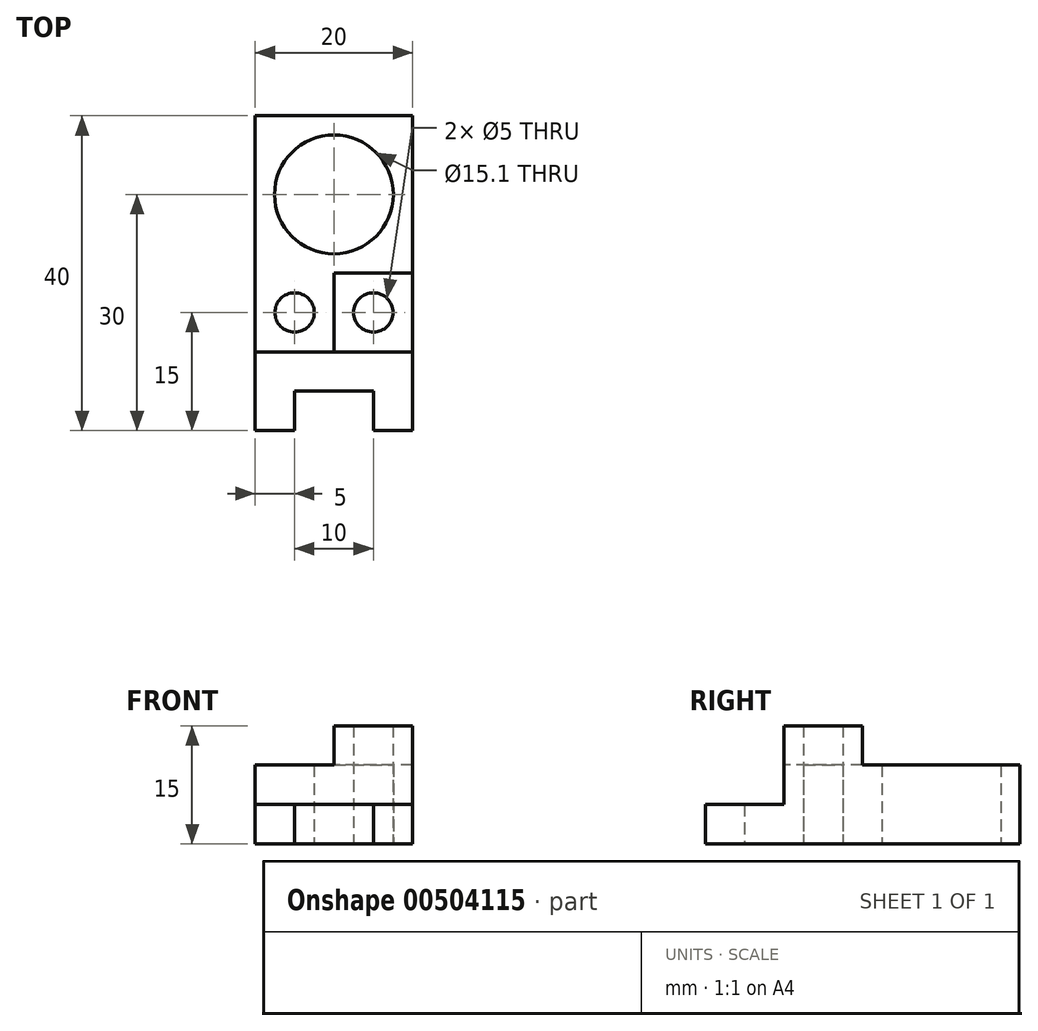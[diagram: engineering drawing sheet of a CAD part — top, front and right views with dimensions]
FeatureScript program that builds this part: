
annotation { "Feature Type Name" : "Feature", "Feature Type Description" : "" }
export const myFeature = defineFeature(function(context is Context, id is Id, definition is map)
    precondition{}
    {
        {
            var Q0;
            Q0=qCreatedBy(makeId("Top.planeOp"),FACE);
            var sketch = newSketch(context, id + "F0", { "sketchPlane" : qUnion([Q0])});
            skLineSegment(sketch, "E0.bottom", {"start": v(10, 10) * mm, "end": v(-10, 10) * mm});
            skLineSegment(sketch, "E0.top", {"start": v(10, -10) * mm, "end": v(-10, -10) * mm});
            skLineSegment(sketch, "E0.left", {"start": v(10, 10) * mm, "end": v(10, -10) * mm});
            skLineSegment(sketch, "E0.right", {"start": v(-10, 10) * mm, "end": v(-10, -10) * mm});
            skPoint(sketch, "E0.middle", {"position": v(0, 0) * mm});
            skCircle(sketch, "E1", {"center": v(0, 0) * mm, "radius": 7.55 * mm});
            skLineSegment(sketch, "E2", {"start": v(-10, -10) * mm, "end": v(-10, -20) * mm});
            skLineSegment(sketch, "E3", {"start": v(-10, -20) * mm, "end": v(10, -20) * mm});
            skLineSegment(sketch, "E4", {"start": v(10, -20) * mm, "end": v(10, -10) * mm});
            skLineSegment(sketch, "E5", {"start": v(0, -10) * mm, "end": v(0, -20) * mm});
            skLineSegment(sketch, "E6", {"start": v(-10, -20) * mm, "end": v(-10, -30) * mm});
            skLineSegment(sketch, "E7", {"start": v(-10, -30) * mm, "end": v(-5, -30) * mm});
            skLineSegment(sketch, "E8", {"start": v(-5, -30) * mm, "end": v(-5, -25) * mm});
            skLineSegment(sketch, "E9", {"start": v(-5, -25) * mm, "end": v(5, -25) * mm});
            skLineSegment(sketch, "E10", {"start": v(5, -25) * mm, "end": v(5, -30) * mm});
            skLineSegment(sketch, "E11", {"start": v(5, -30) * mm, "end": v(10, -30) * mm});
            skLineSegment(sketch, "E12", {"start": v(10, -30) * mm, "end": v(10, -20) * mm});
            skLineSegment(sketch, "E13", {"start": v(0, -15) * mm, "end": v(5, -15) * mm, "construction": true});
            skCircle(sketch, "E14", {"center": v(5, -15) * mm, "radius": 2.5 * mm});
            skCircle(sketch, "E15.MirrorC", {"center": v(-5, -15) * mm, "radius": 2.5 * mm});
            skSolve(sketch);
        }
        {
            var Q0;
            Q0=makeQuery(id+"F0.imprint","IMPRINT",FACE,{"disambiguationData":[TD([[makeQuery(id+"F0.imprint","IMPRINT",EDGE,{"derivedFrom":sQuery(id+"F0.wireOp",EDGE,"E0.bottom")}),1.0]])]});
            extrude(context, id + "F1", {"entities" : qUnion([Q0]), "depth" : 10 * mm});
        }
        {
            var Q0;
            {var subQ0=sQuery(id+"F0.wireOp",EDGE,"E2");Q0=makeQuery(id+"F0.imprint","IMPRINT",FACE,{"disambiguationData":[TD([[makeQuery(id+"F0.imprint","IMPRINT",EDGE,{"derivedFrom":subQ0}),1.0]])]});}
            var Q1;
            {var subQ0=sQuery(id+"F0.wireOp",EDGE,"E6");Q1=makeQuery(id+"F0.imprint","IMPRINT",FACE,{"disambiguationData":[TD([[makeQuery(id+"F0.imprint","IMPRINT",EDGE,{"derivedFrom":subQ0}),1.0]])]});}
            var Q2;
            Q2=makeQuery(id+"F0.imprint","IMPRINT",FACE,{"disambiguationData":[TD([[makeQuery(id+"F0.imprint","IMPRINT",EDGE,{"derivedFrom":sQuery(id+"F0.wireOp",EDGE,"E15.MirrorC")}),-1.0]])]});
            extrude(context, id + "F2", {"entities" : qUnion([Q0, Q1, Q2]), "operationType" : NewBodyOperationType.ADD, "depth" : 5 * mm});
        }
        {
            var Q0;
            {var subQ0=sQuery(id+"F0.wireOp",EDGE,"E4");Q0=makeQuery(id+"F0.imprint","IMPRINT",FACE,{"disambiguationData":[TD([[makeQuery(id+"F0.imprint","IMPRINT",EDGE,{"derivedFrom":subQ0}),1.0]])]});}
            extrude(context, id + "F3", {"entities" : qUnion([Q0]), "operationType" : NewBodyOperationType.ADD, "depth" : 15 * mm});
        }
        {
            var Q0;
            Q0=makeQuery(id+"F0.imprint","IMPRINT",FACE,{"disambiguationData":[TD([[makeQuery(id+"F0.imprint","IMPRINT",EDGE,{"derivedFrom":sQuery(id+"F0.wireOp",EDGE,"E15.MirrorC")}),-1.0]])]});
            extrude(context, id + "F4", {"entities" : qUnion([Q0]), "operationType" : NewBodyOperationType.ADD, "depth" : 10 * mm});
        }
    });
